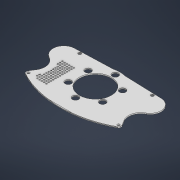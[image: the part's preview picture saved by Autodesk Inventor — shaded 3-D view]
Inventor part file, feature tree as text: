
AUTODESK INVENTOR PART (.ipt)
format: ipt  version: 2022 (Build 260153000, 153)  size: 358,400 bytes
history: native  units: mm
features: sketch x6, extrude x5, projected_geometry x3, chamfer x1, pattern_linear x1, split x1
ambient origin geometry x8: Origin, YZ Plane, XZ Plane, XY Plane, X Axis, Y Axis, Z Axis, Center Point
bodies: Solid1 (feature_tree)
feature tree (17):
  extrude  "Extrusion1"  Depth=2.0mm TaperAngle=0.0deg
  chamfer  "Chamfer1"  Distance=2.0mm Angle=45.0deg
  extrude  "Extrusion2"  Depth=4.0mm
  pattern_linear  "Rectangular Pattern1"  Count1=13 Spacing1=4.0mm
  extrude  "Extrusion3"  Depth=6.0mm
  extrude  "Extrusion4"  Depth=10.0mm
  split  "Split1"
  extrude  "Extrusion6"  TaperAngle=45.0deg  [1 undecoded]
  sketch  "Sketch1"  dims[d0=1.5mm d1=2.5mm d3=3.0mm d4=4.0mm d6=1.0mm d7=90.0deg d8=2.0mm d9=0.0mm d10=0.75mm d11=2.0mm d12=45.0deg]
  sketch  "Sketch2"  dims[d15=2.5mm d16=4.0mm]
  sketch  "Sketch3"  dims[d17=4.0mm]
  sketch  "Sketch4"  dims[d18=0.0mm d19=0.0mm d20=130.0mm d22=4.0mm d23=60.0mm d25=4.0mm]
  sketch  "Sketch5"  dims[d26=10.0mm d27=6.0mm]
  projected_geometry  "Projected Loop1"
  projected_geometry  "Projected Loop2"
  sketch  "Sketch7"  dims[d28=10.0mm d29=0.0mm d31=1.0mm d32=45.0deg d33=100.0mm d34=0.0mm d37=5.0mm d38=0.0mm]
  projected_geometry  "Projected Loop5"
note: 1 required parameter value undecoded (feature->parameter linkage not recoverable at this tier; creation-order binding heuristic only, values carry confidence <= 0.55)
